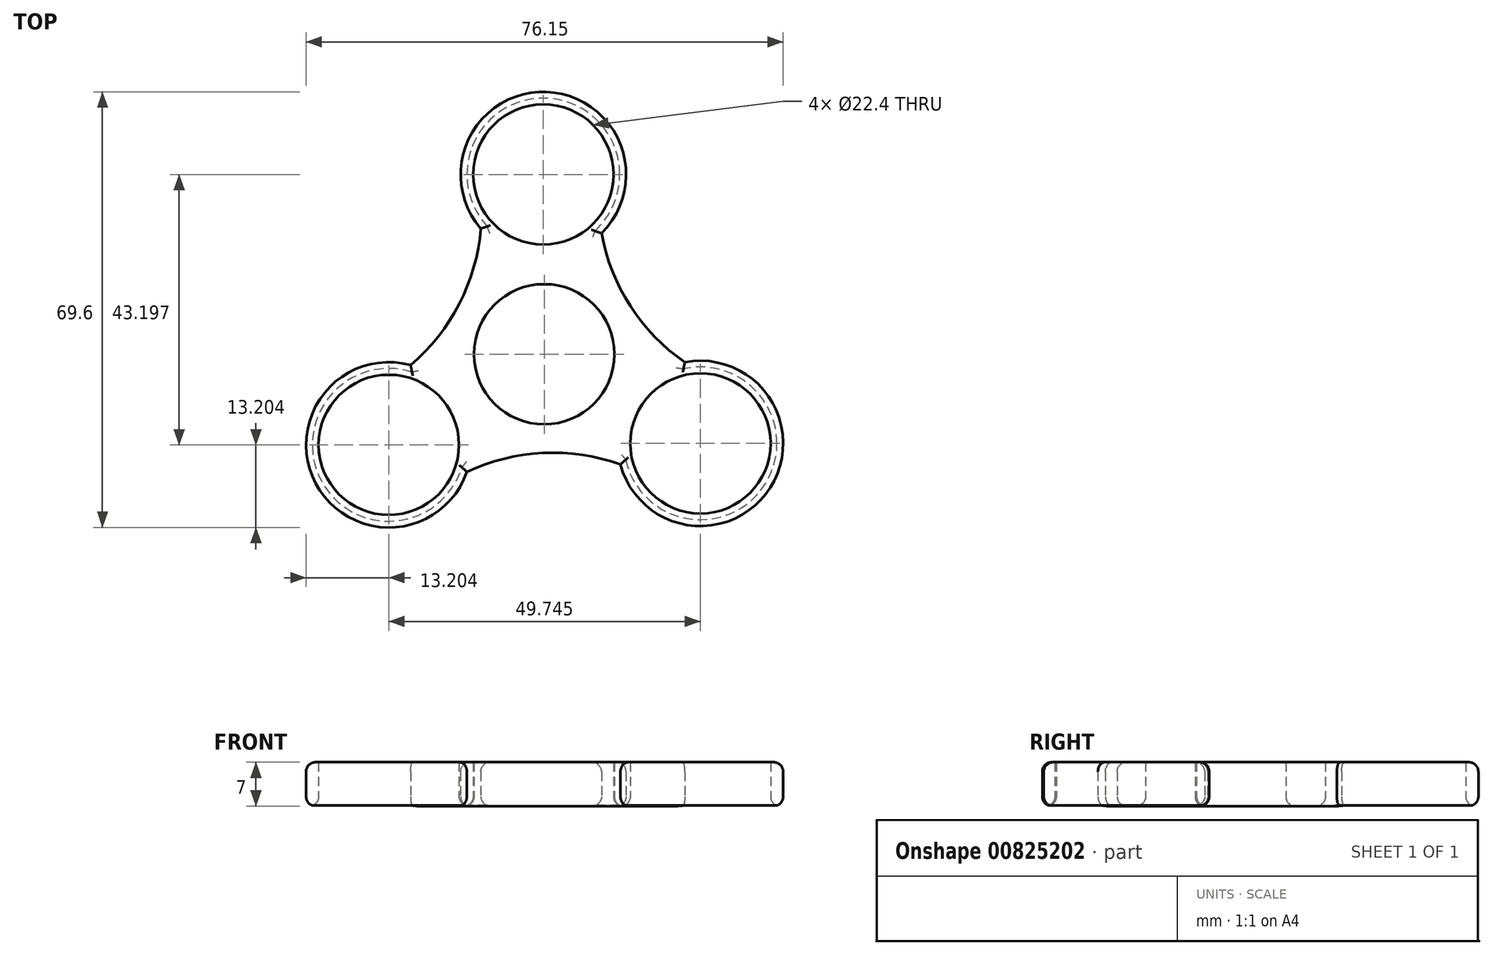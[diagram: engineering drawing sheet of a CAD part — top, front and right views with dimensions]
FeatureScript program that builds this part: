
annotation { "Feature Type Name" : "Feature", "Feature Type Description" : "" }
export const myFeature = defineFeature(function(context is Context, id is Id, definition is map)
    precondition{}
    {
        {
            var Q0;
            Q0=qCreatedBy(makeId("Top.planeOp"),FACE);
            var sketch = newSketch(context, id + "F0", { "sketchPlane" : qUnion([Q0])});
            skCircle(sketch, "E0", {"center": v(0, 0) * mm, "radius": 11.2 * mm});
            skCircle(sketch, "E1", {"center": v(-0.13, 28.72) * mm, "radius": 11.2 * mm});
            skArc(sketch, "E2", {"start": v(9.15, 19.34) * mm, "mid": v(0.37, 41.91) * mm, "end": v(-10.11, 20.08) * mm});
            skCircle(sketch, "E3.1.0", {"center": v(-24.8, -14.48) * mm, "radius": 11.2 * mm});
            skArc(sketch, "E3.1.1", {"start": v(-21.33, -1.74) * mm, "mid": v(-36.48, -20.63) * mm, "end": v(-12.33, -18.8) * mm});
            skCircle(sketch, "E3.2.0", {"center": v(24.94, -14.24) * mm, "radius": 11.2 * mm});
            skArc(sketch, "E3.2.1", {"start": v(12.17, -17.6) * mm, "mid": v(36.1, -21.28) * mm, "end": v(22.45, -1.28) * mm});
            skArc(sketch, "E4", {"start": v(9.15, 19.34) * mm, "mid": v(13.75, 7.7) * mm, "end": v(22.45, -1.28) * mm});
            skArc(sketch, "E5.1.0", {"start": v(-21.33, -1.74) * mm, "mid": v(-13.55, 8.05) * mm, "end": v(-10.11, 20.08) * mm});
            skArc(sketch, "E5.2.0", {"start": v(12.17, -17.6) * mm, "mid": v(-0.2, -15.76) * mm, "end": v(-12.33, -18.8) * mm});
            skSolve(sketch);
        }
        {
            var Q0;
            Q0 = qSketchRegion(id + "F0", true);
            extrude(context, id + "F1", {"entities" : qUnion([Q0]), "depth" : 7 * mm, "offsetDistance" : 25 * mm});
        }
        {
            var Q0;
            Q0=makeQuery(id+"F1.opExtrude","CAP_EDGE",EDGE,{"disambiguationData":[OSD([sQuery(id+"F0.wireOp",EDGE,"E5.2.0")])],"isStart":false});
            fillet(context, id + "F2", {"entities" : qUnion([Q0]), "radius" : 1.5 * mm, "tangentPropagation" : true, "allowEdgeOverflow" : false});
        }
        {
            var Q0;
            Q0=makeQuery(id+"F1.opExtrude","CAP_EDGE",EDGE,{"disambiguationData":[OSD([sQuery(id+"F0.wireOp",EDGE,"E3.1.1")])],"isStart":false});
            var Q1;
            Q1=makeQuery(id+"F1.opExtrude","CAP_EDGE",EDGE,{"disambiguationData":[OSD([sQuery(id+"F0.wireOp",EDGE,"E5.1.0")])],"isStart":false});
            var Q2;
            Q2=makeQuery(id+"F1.opExtrude","CAP_EDGE",EDGE,{"disambiguationData":[OSD([sQuery(id+"F0.wireOp",EDGE,"E3.2.1")])],"isStart":false});
            var Q3;
            Q3=makeQuery(id+"F1.opExtrude","CAP_EDGE",EDGE,{"disambiguationData":[OSD([sQuery(id+"F0.wireOp",EDGE,"E2")])],"isStart":false});
            var Q4;
            Q4=makeQuery(id+"F1.opExtrude","CAP_EDGE",EDGE,{"disambiguationData":[OSD([sQuery(id+"F0.wireOp",EDGE,"E4")])],"isStart":false});
            fillet(context, id + "F3", {"entities" : qUnion([Q0, Q1, Q2, Q3, Q4]), "radius" : 1.5 * mm, "tangentPropagation" : true, "allowEdgeOverflow" : false});
        }
        {
            var Q0;
            Q0=makeQuery(id+"F1.opExtrude","CAP_EDGE",EDGE,{"disambiguationData":[OSD([sQuery(id+"F0.wireOp",EDGE,"E3.2.0")])],"isStart":true});
            var Q1;
            Q1=makeQuery(id+"F1.opExtrude","CAP_EDGE",EDGE,{"disambiguationData":[OSD([sQuery(id+"F0.wireOp",EDGE,"E3.2.1")])],"isStart":true});
            var Q2;
            Q2=makeQuery(id+"F1.opExtrude","CAP_EDGE",EDGE,{"disambiguationData":[OSD([sQuery(id+"F0.wireOp",EDGE,"E4")])],"isStart":true});
            var Q3;
            Q3=makeQuery(id+"F1.opExtrude","CAP_EDGE",EDGE,{"disambiguationData":[OSD([sQuery(id+"F0.wireOp",EDGE,"E2")])],"isStart":true});
            var Q4;
            Q4=makeQuery(id+"F1.opExtrude","CAP_EDGE",EDGE,{"disambiguationData":[OSD([sQuery(id+"F0.wireOp",EDGE,"E5.1.0")])],"isStart":true});
            var Q5;
            Q5=makeQuery(id+"F1.opExtrude","CAP_FACE",FACE,{"disambiguationData":[OSD([sQuery(id+"F0.wireOp",EDGE,"E0"),sQuery(id+"F0.wireOp",EDGE,"E1"),sQuery(id+"F0.wireOp",EDGE,"E2"),sQuery(id+"F0.wireOp",EDGE,"E3.1.0"),sQuery(id+"F0.wireOp",EDGE,"E3.1.1"),sQuery(id+"F0.wireOp",EDGE,"E3.2.0"),sQuery(id+"F0.wireOp",EDGE,"E3.2.1"),sQuery(id+"F0.wireOp",EDGE,"E4"),sQuery(id+"F0.wireOp",EDGE,"E5.1.0"),sQuery(id+"F0.wireOp",EDGE,"E5.2.0")])],"isStart":true});
            var Q6;
            Q6=makeQuery(id+"F1.opExtrude","CAP_EDGE",EDGE,{"disambiguationData":[OSD([sQuery(id+"F0.wireOp",EDGE,"E3.1.1")])],"isStart":true});
            var Q7;
            Q7=makeQuery(id+"F1.opExtrude","CAP_EDGE",EDGE,{"disambiguationData":[OSD([sQuery(id+"F0.wireOp",EDGE,"E3.1.0")])],"isStart":true});
            var Q8;
            Q8=makeQuery(id+"F1.opExtrude","CAP_EDGE",EDGE,{"disambiguationData":[OSD([sQuery(id+"F0.wireOp",EDGE,"E5.2.0")])],"isStart":true});
            fillet(context, id + "F4", {"entities" : qUnion([Q0, Q1, Q2, Q3, Q4, Q5, Q6, Q7, Q8]), "radius" : 1.5 * mm, "tangentPropagation" : true, "allowEdgeOverflow" : false});
        }
    });
